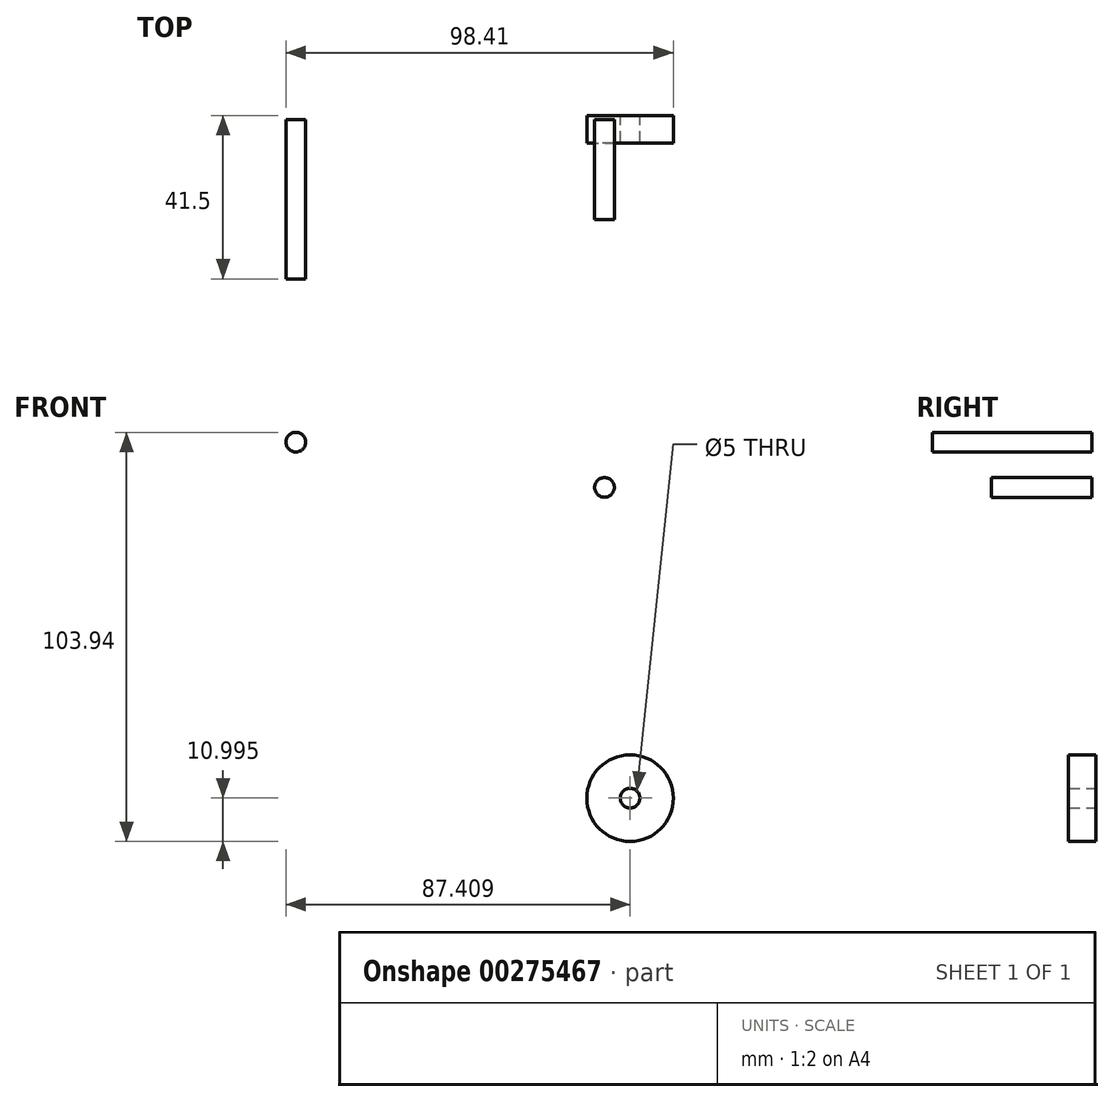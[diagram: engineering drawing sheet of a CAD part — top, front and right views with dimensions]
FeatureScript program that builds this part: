
annotation { "Feature Type Name" : "Feature", "Feature Type Description" : "" }
export const myFeature = defineFeature(function(context is Context, id is Id, definition is map)
    precondition{}
    {
        {
            var Q0;
            Q0=qCreatedBy(makeId("Front.planeOp"),FACE);
            var sketch = newSketch(context, id + "F0", { "sketchPlane" : qUnion([Q0])});
            skCircle(sketch, "E0", {"center": v(48.8, -46.8) * mm, "radius": 11 * mm});
            skCircle(sketch, "E1", {"center": v(48.8, -46.8) * mm, "radius": 2.5 * mm});
            skSolve(sketch);
        }
        {
            var Q0;
            Q0=qSketchRegion(id+"F0",true);
            extrude(context, id + "F1", {"entities" : qUnion([Q0]), "depth" : 6 * mm, "hasSecondDirection" : true, "secondDirectionOppositeDirection" : true, "secondDirectionDepth" : 1 * mm});
        }
        {
            var Q0;
            Q0=qCreatedBy(makeId("Front.planeOp"),FACE);
            var sketch = newSketch(context, id + "F2", { "sketchPlane" : qUnion([Q0])});
            skCircle(sketch, "E2", {"center": v(42.3, 32.16) * mm, "radius": 2.5 * mm});
            skSolve(sketch);
        }
        {
            var Q0;
            Q0=qSketchRegion(id+"F2",true);
            extrude(context, id + "F3", {"entities" : qUnion([Q0]), "depth" : 25.5 * mm});
        }
        {
            var Q0;
            Q0=qCreatedBy(makeId("Front.planeOp"),FACE);
            var sketch = newSketch(context, id + "F4", { "sketchPlane" : qUnion([Q0])});
            skCircle(sketch, "E3", {"center": v(-36.1, 43.65) * mm, "radius": 2.5 * mm});
            skSolve(sketch);
        }
        {
            var Q0;
            Q0=qSketchRegion(id+"F4",true);
            extrude(context, id + "F5", {"entities" : qUnion([Q0]), "depth" : 40.5 * mm});
        }
    });
